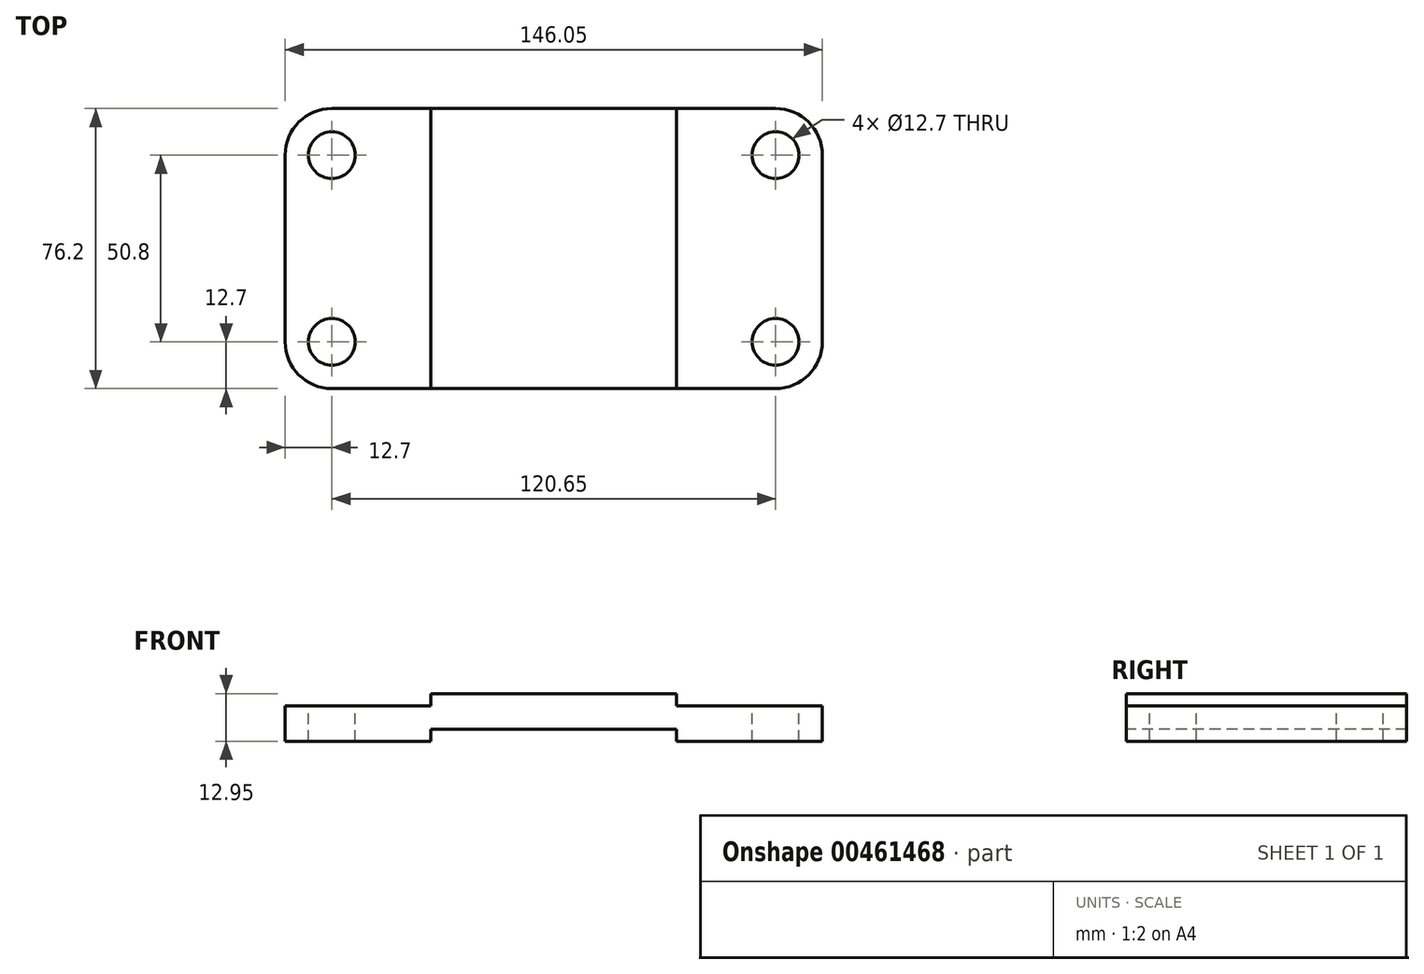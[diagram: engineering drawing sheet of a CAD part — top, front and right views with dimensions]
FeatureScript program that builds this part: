
annotation { "Feature Type Name" : "Feature", "Feature Type Description" : "" }
export const myFeature = defineFeature(function(context is Context, id is Id, definition is map)
    precondition{}
    {
        {
            var Q0;
            Q0=qCreatedBy(makeId("Top.planeOp"),FACE);
            var sketch = newSketch(context, id + "F0", { "sketchPlane" : qUnion([Q0])});
            skLineSegment(sketch, "E0.bottom", {"start": v(0, 0) * mm, "end": v(146.05, 0) * mm});
            skLineSegment(sketch, "E0.top", {"start": v(0, 76.2) * mm, "end": v(146.05, 76.2) * mm});
            skLineSegment(sketch, "E0.left", {"start": v(0, 0) * mm, "end": v(0, 76.2) * mm});
            skLineSegment(sketch, "E0.right", {"start": v(146.05, 0) * mm, "end": v(146.05, 76.2) * mm});
            skSolve(sketch);
        }
        {
            var Q0;
            Q0=makeQuery(id+"F0.imprint","IMPRINT",FACE,{"disambiguationData":[TD([[makeQuery(id+"F0.imprint","IMPRINT",EDGE,{"derivedFrom":sQuery(id+"F0.wireOp",EDGE,"E0.bottom")}),1.0]])]});
            extrude(context, id + "F1", {"entities" : qUnion([Q0]), "depth" : 12.95 * mm});
        }
        {
            var Q0;
            Q0=makeQuery(id+"F1.opExtrude","SWEPT_FACE",FACE,{"disambiguationData":[OSD([sQuery(id+"F0.wireOp",EDGE,"E0.bottom")])]});
            var sketch = newSketch(context, id + "F2", { "sketchPlane" : qUnion([Q0])});
            skLineSegment(sketch, "E1.bottom", {"start": v(0, 12.95) * mm, "end": v(39.62, 12.95) * mm});
            skLineSegment(sketch, "E1.top", {"start": v(0, 9.65) * mm, "end": v(39.62, 9.65) * mm});
            skLineSegment(sketch, "E1.left", {"start": v(0, 12.95) * mm, "end": v(0, 9.65) * mm});
            skLineSegment(sketch, "E1.right", {"start": v(39.62, 12.95) * mm, "end": v(39.62, 9.65) * mm});
            skLineSegment(sketch, "E2.bottom", {"start": v(146.05, 12.95) * mm, "end": v(106.43, 12.95) * mm});
            skLineSegment(sketch, "E2.top", {"start": v(146.05, 9.65) * mm, "end": v(106.43, 9.65) * mm});
            skLineSegment(sketch, "E2.left", {"start": v(146.05, 12.95) * mm, "end": v(146.05, 9.65) * mm});
            skLineSegment(sketch, "E2.right", {"start": v(106.43, 12.95) * mm, "end": v(106.43, 9.65) * mm});
            skSolve(sketch);
        }
        {
            var Q0;
            Q0=makeQuery(id+"F2.imprint","IMPRINT",FACE,{"disambiguationData":[TD([[makeQuery(id+"F2.imprint","IMPRINT",EDGE,{"derivedFrom":sQuery(id+"F2.wireOp",EDGE,"E2.bottom")}),-1.0]])]});
            var Q1;
            Q1=makeQuery(id+"F2.imprint","IMPRINT",FACE,{"disambiguationData":[TD([[makeQuery(id+"F2.imprint","IMPRINT",EDGE,{"derivedFrom":sQuery(id+"F2.wireOp",EDGE,"E1.bottom")}),-1.0]])]});
            extrude(context, id + "F3", {"entities" : qUnion([Q0, Q1]), "operationType" : NewBodyOperationType.REMOVE, "endBound" : BoundingType.THROUGH_ALL, "oppositeDirection" : true, "depth" : 25.4 * mm});
        }
        {
            var Q0;
            Q0=makeQuery(id+"F1.opExtrude","SWEPT_FACE",FACE,{"disambiguationData":[OSD([sQuery(id+"F0.wireOp",EDGE,"E0.bottom")])]});
            var sketch = newSketch(context, id + "F4", { "sketchPlane" : qUnion([Q0])});
            skLineSegment(sketch, "E3.bottom", {"start": v(39.62, 0) * mm, "end": v(106.43, 0) * mm});
            skLineSegment(sketch, "E3.top", {"start": v(39.62, 3.3) * mm, "end": v(106.43, 3.3) * mm});
            skLineSegment(sketch, "E3.left", {"start": v(39.62, 0) * mm, "end": v(39.62, 3.3) * mm});
            skLineSegment(sketch, "E3.right", {"start": v(106.43, 0) * mm, "end": v(106.43, 3.3) * mm});
            skSolve(sketch);
        }
        {
            var Q0;
            Q0=makeQuery(id+"F4.imprint","IMPRINT",FACE,{"disambiguationData":[TD([[makeQuery(id+"F4.imprint","IMPRINT",EDGE,{"derivedFrom":sQuery(id+"F4.wireOp",EDGE,"E3.bottom")}),1.0]])]});
            extrude(context, id + "F5", {"entities" : qUnion([Q0]), "operationType" : NewBodyOperationType.REMOVE, "endBound" : BoundingType.THROUGH_ALL, "oppositeDirection" : true, "depth" : 25.4 * mm});
        }
        {
            var Q0;
            Q0=makeQuery(id+"F1.opExtrude","SWEPT_EDGE",EDGE,{"disambiguationData":[OSD([sQuery(id+"F0.wireOp",EDGE,"E0.bottom"),sQuery(id+"F0.wireOp",EDGE,"E0.left")])]});
            var Q1;
            Q1=makeQuery(id+"F1.opExtrude","SWEPT_EDGE",EDGE,{"disambiguationData":[OSD([sQuery(id+"F0.wireOp",EDGE,"E0.top"),sQuery(id+"F0.wireOp",EDGE,"E0.left")])]});
            var Q2;
            Q2=makeQuery(id+"F1.opExtrude","SWEPT_EDGE",EDGE,{"disambiguationData":[OSD([sQuery(id+"F0.wireOp",EDGE,"E0.top"),sQuery(id+"F0.wireOp",EDGE,"E0.right")])]});
            var Q3;
            Q3=makeQuery(id+"F1.opExtrude","SWEPT_EDGE",EDGE,{"disambiguationData":[OSD([sQuery(id+"F0.wireOp",EDGE,"E0.bottom"),sQuery(id+"F0.wireOp",EDGE,"E0.right")])]});
            fillet(context, id + "F6", {"entities" : qUnion([Q0, Q1, Q2, Q3]), "radius" : 12.7 * mm, "tangentPropagation" : true, "allowEdgeOverflow" : false});
        }
        {
            var Q0;
            Q0=makeQuery(id+"F3.boolean.opBoolean","COPY",FACE,{"derivedFrom":makeQuery(id+"F3.opExtrude","SWEPT_FACE",FACE,{"disambiguationData":[OSD([sQuery(id+"F2.wireOp",EDGE,"E1.top")])]})});
            var sketch = newSketch(context, id + "F7", { "sketchPlane" : qUnion([Q0])});
            skLineSegment(sketch, "E4.bottom", {"start": v(0, 0) * mm, "end": v(12.7, 0) * mm});
            skLineSegment(sketch, "E4.top", {"start": v(0, 12.7) * mm, "end": v(12.7, 12.7) * mm});
            skLineSegment(sketch, "E4.left", {"start": v(0, 0) * mm, "end": v(0, 12.7) * mm});
            skLineSegment(sketch, "E4.right", {"start": v(12.7, 0) * mm, "end": v(12.7, 12.7) * mm});
            skCircle(sketch, "E5", {"center": v(12.7, 12.7) * mm, "radius": 6.35 * mm});
            skCircle(sketch, "E6", {"center": v(12.7, 63.5) * mm, "radius": 6.35 * mm});
            skSolve(sketch);
        }
        {
            var Q0;
            Q0=makeQuery(id+"F3.boolean.opBoolean","COPY",FACE,{"derivedFrom":makeQuery(id+"F3.opExtrude","SWEPT_FACE",FACE,{"disambiguationData":[OSD([sQuery(id+"F2.wireOp",EDGE,"E2.top")])]})});
            var sketch = newSketch(context, id + "F8", { "sketchPlane" : qUnion([Q0])});
            skLineSegment(sketch, "E7", {"start": v(146.05, 63.5) * mm, "end": v(133.35, 63.5) * mm});
            skLineSegment(sketch, "E8", {"start": v(133.35, 63.5) * mm, "end": v(133.35, 12.7) * mm});
            skCircle(sketch, "E9", {"center": v(133.35, 63.5) * mm, "radius": 6.35 * mm});
            skCircle(sketch, "E10", {"center": v(133.35, 12.7) * mm, "radius": 6.35 * mm});
            skSolve(sketch);
        }
        {
            var Q0;
            {var subQ0=sQuery(id+"F8.wireOp",EDGE,"E8");var subQ1=sQuery(id+"F8.wireOp",EDGE,"E7");var subQ2=makeQuery(id+"F8.imprint","INTERSECT",VERTEX,{"derivedFrom":[subQ1,subQ0]});Q0=makeQuery(id+"F8.imprint","IMPRINT",FACE,{"disambiguationData":[TD([[makeQuery(id+"F8.imprint","IMPRINT",EDGE,{"disambiguationData":[TD([[subQ2,1.0]])],"derivedFrom":subQ1}),-1.0]])]});}
            var Q1;
            {var subQ0=sQuery(id+"F8.wireOp",EDGE,"E8");var subQ1=sQuery(id+"F8.wireOp",EDGE,"E7");var subQ2=makeQuery(id+"F8.imprint","INTERSECT",VERTEX,{"derivedFrom":[subQ1,subQ0]});Q1=makeQuery(id+"F8.imprint","IMPRINT",FACE,{"disambiguationData":[TD([[makeQuery(id+"F8.imprint","IMPRINT",EDGE,{"disambiguationData":[TD([[subQ2,1.0]])],"derivedFrom":subQ1}),1.0]])]});}
            var Q2;
            Q2=makeQuery(id+"F8.imprint","IMPRINT",FACE,{"disambiguationData":[TD([[makeQuery(id+"F8.imprint","IMPRINT",EDGE,{"derivedFrom":sQuery(id+"F8.wireOp",EDGE,"E10")}),1.0]])]});
            var Q3;
            Q3=makeQuery(id+"F7.imprint","IMPRINT",FACE,{"disambiguationData":[TD([[makeQuery(id+"F7.imprint","IMPRINT",EDGE,{"derivedFrom":sQuery(id+"F7.wireOp",EDGE,"E6")}),1.0]])]});
            var Q4;
            {var subQ0=sQuery(id+"F7.wireOp",EDGE,"E4.right");var subQ1=sQuery(id+"F7.wireOp",EDGE,"E4.top");var subQ2=makeQuery(id+"F7.imprint","INTERSECT",VERTEX,{"derivedFrom":[subQ1,subQ0]});Q4=makeQuery(id+"F7.imprint","IMPRINT",FACE,{"disambiguationData":[TD([[makeQuery(id+"F7.imprint","IMPRINT",EDGE,{"disambiguationData":[TD([[subQ2,1.0]])],"derivedFrom":subQ1}),1.0]])]});}
            var Q5;
            {var subQ0=sQuery(id+"F7.wireOp",EDGE,"E4.right");var subQ1=sQuery(id+"F7.wireOp",EDGE,"E4.top");var subQ2=makeQuery(id+"F7.imprint","INTERSECT",VERTEX,{"derivedFrom":[subQ1,subQ0]});Q5=makeQuery(id+"F7.imprint","IMPRINT",FACE,{"disambiguationData":[TD([[makeQuery(id+"F7.imprint","IMPRINT",EDGE,{"disambiguationData":[TD([[subQ2,1.0]])],"derivedFrom":subQ1}),-1.0]])]});}
            extrude(context, id + "F9", {"entities" : qUnion([Q0, Q1, Q2, Q3, Q4, Q5]), "operationType" : NewBodyOperationType.REMOVE, "endBound" : BoundingType.THROUGH_ALL, "oppositeDirection" : true, "depth" : 25.4 * mm});
        }
    });
